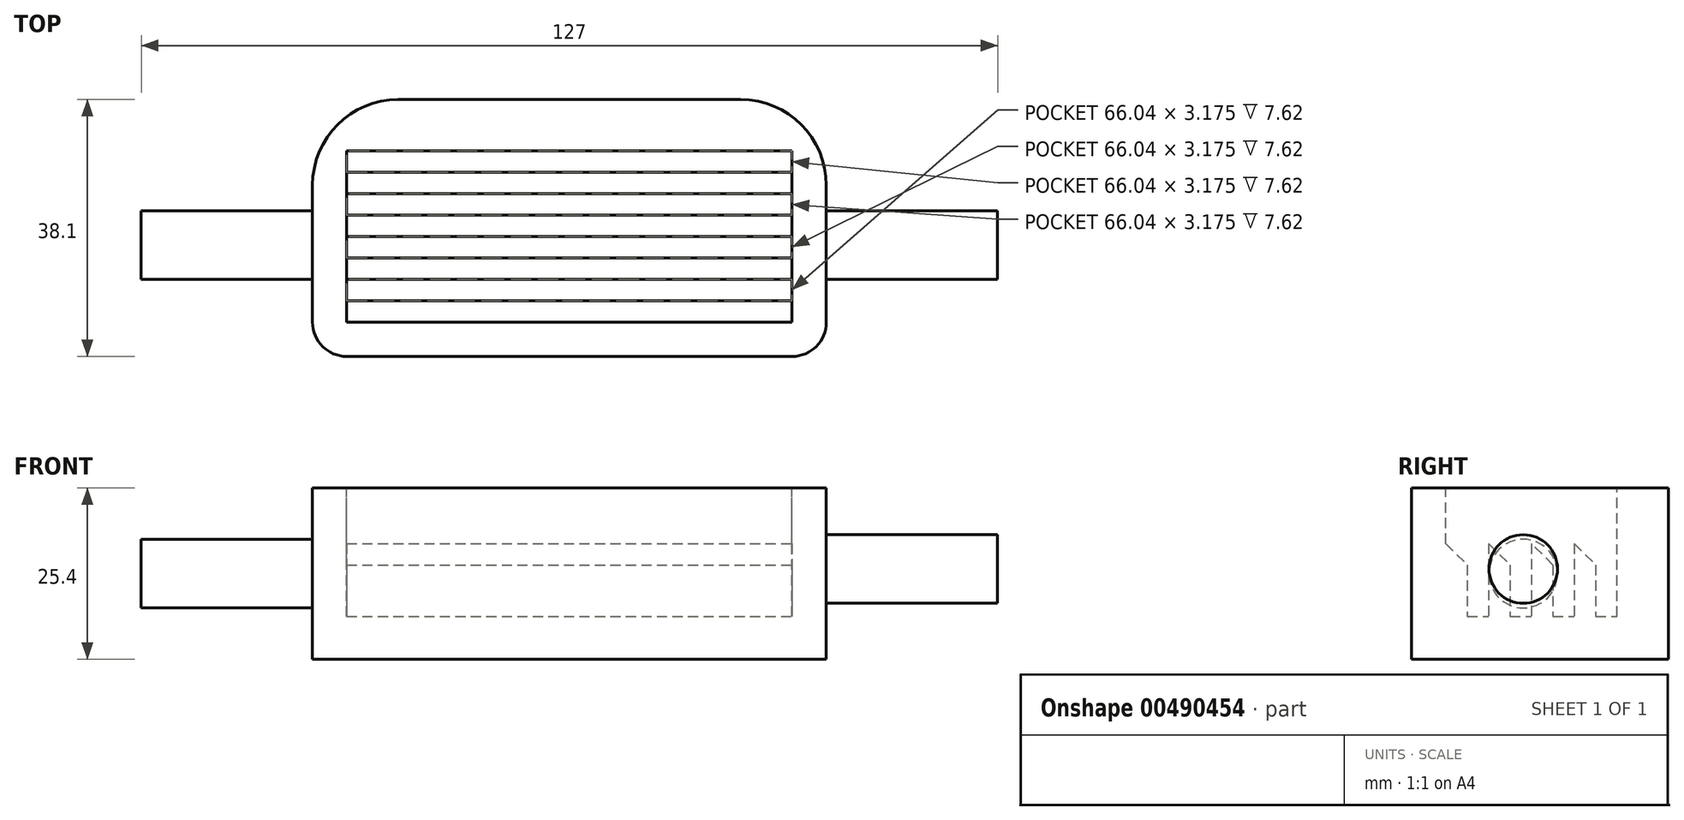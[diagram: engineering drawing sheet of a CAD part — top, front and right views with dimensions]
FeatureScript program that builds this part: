
annotation { "Feature Type Name" : "Feature", "Feature Type Description" : "" }
export const myFeature = defineFeature(function(context is Context, id is Id, definition is map)
    precondition{}
    {
        {
            var Q0;
            Q0=qCreatedBy(makeId("Top.planeOp"),FACE);
            var sketch = newSketch(context, id + "F0", { "sketchPlane" : qUnion([Q0])});
            skLineSegment(sketch, "E0.bottom", {"start": v(-39.8, 21.56) * mm, "end": v(36.4, 21.56) * mm});
            skLineSegment(sketch, "E0.top", {"start": v(-39.8, -16.54) * mm, "end": v(36.4, -16.54) * mm});
            skLineSegment(sketch, "E0.left", {"start": v(-39.8, 21.56) * mm, "end": v(-39.8, -16.54) * mm});
            skLineSegment(sketch, "E0.right", {"start": v(36.4, 21.56) * mm, "end": v(36.4, -16.54) * mm});
            skSolve(sketch);
        }
        {
            var Q0;
            Q0 = qSketchRegion(id + "F0", true);
            extrude(context, id + "F1", {"entities" : qUnion([Q0]), "depth" : 25.4 * mm});
        }
        {
            var Q0;
            Q0=makeQuery(id+"F1.opExtrude","SWEPT_EDGE",EDGE,{"disambiguationData":[OSD([sQuery(id+"F0.wireOp",EDGE,"E0.bottom"),sQuery(id+"F0.wireOp",EDGE,"E0.left")])]});
            var Q1;
            Q1=makeQuery(id+"F1.opExtrude","SWEPT_EDGE",EDGE,{"disambiguationData":[OSD([sQuery(id+"F0.wireOp",EDGE,"E0.bottom"),sQuery(id+"F0.wireOp",EDGE,"E0.right")])]});
            fillet(context, id + "F2", {"entities" : qUnion([Q0, Q1]), "radius" : 12.7 * mm, "tangentPropagation" : true, "allowEdgeOverflow" : false});
        }
        {
            var Q0;
            Q0=makeQuery(id+"F1.opExtrude","SWEPT_EDGE",EDGE,{"disambiguationData":[OSD([sQuery(id+"F0.wireOp",EDGE,"E0.top"),sQuery(id+"F0.wireOp",EDGE,"E0.left")])]});
            var Q1;
            Q1=makeQuery(id+"F1.opExtrude","SWEPT_EDGE",EDGE,{"disambiguationData":[OSD([sQuery(id+"F0.wireOp",EDGE,"E0.top"),sQuery(id+"F0.wireOp",EDGE,"E0.right")])]});
            fillet(context, id + "F3", {"entities" : qUnion([Q0, Q1]), "radius" : 5.08 * mm, "tangentPropagation" : true, "allowEdgeOverflow" : false});
        }
        {
            var Q0;
            Q0=makeQuery(id+"F1.opExtrude","SWEPT_FACE",FACE,{"disambiguationData":[OSD([sQuery(id+"F0.wireOp",EDGE,"E0.left")])]});
            var sketch = newSketch(context, id + "F4", { "sketchPlane" : qUnion([Q0])});
            skCircle(sketch, "E1", {"center": v(0, 12.7) * mm, "radius": 5.08 * mm});
            skPoint(sketch, "E1.centerSnap0", {"position": v(-8.86, 12.7) * mm});
            skSolve(sketch);
        }
        {
            var Q0;
            Q0 = qSketchRegion(id + "F4", true);
            extrude(context, id + "F5", {"entities" : qUnion([Q0]), "operationType" : NewBodyOperationType.ADD, "depth" : 25.4 * mm});
        }
        {
            var Q0;
            Q0=makeQuery(id+"F1.opExtrude","SWEPT_FACE",FACE,{"disambiguationData":[OSD([sQuery(id+"F0.wireOp",EDGE,"E0.right")])]});
            var sketch = newSketch(context, id + "F6", { "sketchPlane" : qUnion([Q0])});
            skCircle(sketch, "E2", {"center": v(0, 13.39) * mm, "radius": 5.08 * mm});
            skSolve(sketch);
        }
        {
            var Q0;
            Q0 = qSketchRegion(id + "F6", true);
            extrude(context, id + "F7", {"entities" : qUnion([Q0]), "operationType" : NewBodyOperationType.ADD, "depth" : 25.4 * mm});
        }
        {
            var Q0;
            Q0=makeQuery(id+"F1.opExtrude","CAP_FACE",FACE,{"disambiguationData":[OSD([sQuery(id+"F0.wireOp",EDGE,"E0.bottom"),sQuery(id+"F0.wireOp",EDGE,"E0.top"),sQuery(id+"F0.wireOp",EDGE,"E0.left"),sQuery(id+"F0.wireOp",EDGE,"E0.right")])],"isStart":false});
            var sketch = newSketch(context, id + "F8", { "sketchPlane" : qUnion([Q0])});
            skLineSegment(sketch, "E3", {"start": v(-34.72, -11.46) * mm, "end": v(-34.72, 13.94) * mm});
            skLineSegment(sketch, "E4", {"start": v(31.32, -11.46) * mm, "end": v(31.32, 13.94) * mm});
            skLineSegment(sketch, "E5", {"start": v(31.32, 13.94) * mm, "end": v(-34.72, 13.94) * mm});
            skLineSegment(sketch, "E6", {"start": v(-34.72, -11.46) * mm, "end": v(31.32, -11.46) * mm});
            skSolve(sketch);
        }
        {
            var Q0;
            Q0 = qSketchRegion(id + "F8", true);
            extrude(context, id + "F9", {"entities" : qUnion([Q0]), "operationType" : NewBodyOperationType.REMOVE, "oppositeDirection" : true, "depth" : 19.05 * mm});
        }
        {
            var Q0;
            Q0=makeQuery(id+"F9.boolean.opBoolean","COPY",FACE,{"derivedFrom":makeQuery(id+"F9.opExtrude","CAP_FACE",FACE,{"disambiguationData":[OSD([sQuery(id+"F8.wireOp",EDGE,"E3"),sQuery(id+"F8.wireOp",EDGE,"E4"),sQuery(id+"F8.wireOp",EDGE,"E5"),sQuery(id+"F8.wireOp",EDGE,"E6")])],"isStart":false})});
            var sketch = newSketch(context, id + "F10", { "sketchPlane" : qUnion([Q0])});
            skLineSegment(sketch, "E7", {"start": v(-34.72, 1.24) * mm, "end": v(31.32, 1.24) * mm});
            skLineSegment(sketch, "E8", {"start": v(-34.72, 7.59) * mm, "end": v(31.32, 7.59) * mm});
            skLineSegment(sketch, "E9", {"start": v(-34.72, -5.11) * mm, "end": v(31.32, -5.11) * mm});
            skLineSegment(sketch, "E10", {"start": v(-34.72, 10.76) * mm, "end": v(31.32, 10.76) * mm});
            skLineSegment(sketch, "E11", {"start": v(31.32, 4.41) * mm, "end": v(-34.72, 4.41) * mm});
            skLineSegment(sketch, "E12", {"start": v(-34.72, -1.94) * mm, "end": v(31.32, -1.94) * mm});
            skLineSegment(sketch, "E13", {"start": v(-34.72, -8.29) * mm, "end": v(31.32, -8.29) * mm});
            skSolve(sketch);
        }
        {
            var Q0;
            {var subQ0=sQuery(id+"F10.wireOp",EDGE,"E8");Q0=makeQuery(id+"F10.imprint","IMPRINT",FACE,{"disambiguationData":[TD([[makeQuery(id+"F10.imprint","IMPRINT",EDGE,{"derivedFrom":subQ0}),1.0]])]});}
            var Q1;
            {var subQ0=sQuery(id+"F10.wireOp",EDGE,"E7");Q1=makeQuery(id+"F10.imprint","IMPRINT",FACE,{"disambiguationData":[TD([[makeQuery(id+"F10.imprint","IMPRINT",EDGE,{"derivedFrom":subQ0}),1.0]])]});}
            var Q2;
            {var subQ0=sQuery(id+"F10.wireOp",EDGE,"E9");Q2=makeQuery(id+"F10.imprint","IMPRINT",FACE,{"disambiguationData":[TD([[makeQuery(id+"F10.imprint","IMPRINT",EDGE,{"derivedFrom":subQ0}),1.0]])]});}
            var Q3;
            {var subQ0=sQuery(id+"F10.wireOp",EDGE,"E13");Q3=makeQuery(id+"F10.imprint","IMPRINT",FACE,{"disambiguationData":[TD([[makeQuery(id+"F10.imprint","IMPRINT",EDGE,{"derivedFrom":subQ0}),-1.0]])]});}
            extrude(context, id + "F11", {"entities" : qUnion([Q0, Q1, Q2, Q3]), "operationType" : NewBodyOperationType.ADD, "depth" : 12.7 * mm});
        }
        {
            var Q0;
            Q0=makeQuery(id+"F11.opExtrude","CAP_EDGE",EDGE,{"disambiguationData":[OSD([sQuery(id+"F10.wireOp",EDGE,"E10")])],"isStart":false});
            var Q1;
            Q1=makeQuery(id+"F11.opExtrude","CAP_EDGE",EDGE,{"disambiguationData":[OSD([sQuery(id+"F10.wireOp",EDGE,"E11")])],"isStart":false});
            var Q2;
            Q2=makeQuery(id+"F11.opExtrude","CAP_EDGE",EDGE,{"disambiguationData":[OSD([sQuery(id+"F10.wireOp",EDGE,"E12")])],"isStart":false});
            var Q3;
            Q3=makeQuery(id+"F11.opExtrude","CAP_EDGE",EDGE,{"disambiguationData":[OSD([sQuery(id+"F10.wireOp",EDGE,"E13")])],"isStart":false});
            chamfer(context, id + "F12", {"entities" : qUnion([Q0, Q1, Q2, Q3]), "width" : 5.08 * mm, "tangentPropagation" : true});
        }
    });
